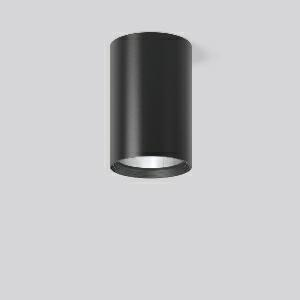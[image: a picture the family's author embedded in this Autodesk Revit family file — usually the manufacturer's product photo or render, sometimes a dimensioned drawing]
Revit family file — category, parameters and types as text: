
# Revit family: heledon_maxi_a_931230_003_4984
name_source: partatom
category: Lighting Fixtures
units: mm (PartAtom-declared; Revit-internal decimal feet)

## family parameters
Cut with Voids When Loaded = No
Host = Face
Light Source = No
Part Type = Normal
Room Calculation Point = No
Round Connector Dimension = Use Diameter
Shared = No

## types (1)
- HELEDON maxi A (1 x LED Modul 932 fresh meat, 2100 lm, 3200)
    Apparent Load = 33 VA
    Approval mark = CE
    CIE Flux Codes = 100 100 100 100 100
    Color Rendering = 90
    Color Temperature = 3200
    Default Elevation = 1800 mm
    Description = Series: HELEDON maxi
Cylindrical surface-mounted downlight. Housing: die-cast aluminium, powder-coated. Internal ceiling frame polycarbonate with bayonet mounting. Black plastic ring and recessed LED to prevent glare from the side. Optical assembly with reflector made of MIRO-Silver with 98% total light reflection for outstanding efficiency - can be changed without tools. Special LED for illumination of meat included. Suitable for Ceiling mounting. Easy installation with a separate ceiling frame with bayonet mounting and plug connection. Driver integrated. Connected via plug-in connector. High quality converter without flickering and stroboscopic effect. The following accessories can be mounted without use of tools: interchangeable lenses, decorative glasses, honeycomb louvre, clear and frosted diffusers, white interchangeable plastic ring. 
Colour: deep black, matt (RAL 9005)
Diameter: 123 mm
Height: 183 mm
Lamp: LED
Socket: without socket
Colour temperature: fresh meat
System power: 33 W
Rated luminous flux: 2100 lm
Luminous efficiency: 64 lm/W
Control gear: Regulated power supply
Protection class: I
Type of protection: IP 20
    Height = 183 mm
    Lamp = 1 x LED Modul 932 fresh meat
    Lamp Light Flux = 2100 lm
    Lamp count = 1
    Length = 123 mm
    Lifetime = 50000 h
    Luminous efficacy = 64 lm/W
    Manufacturer = RZB
    ModVariant = No
    Model = 931230.003
    Mounting Place = Ceiling
    Mounting Type = Surface mounted
    Number of Poles = 1
    OnlyDefault = Yes
    Power Factor = 1
    Product Name = HELEDON maxi A
    Product group = Surface mounted downlights
    ProductGroupID = 302
    Protection Class = Protection class I
    Protection Degree = IP 20
    RLX_Detail_Level = 1
    RLX_Emergency_Light_Flux = 0 lm
    RLX_Emergency_Type = 0
    RLX_Emergency_Type_DB = No
    RlxData = <blob elided: 96753 chars, md5=6b479a37>
    Socket = socket
    Standby Power = 0 W
    System Light Flux = 2100 lm
    System Power = 33 W
    Type Comments = Product without accessories
    Type Image = 931192.003.jpg
    URL = http://relux.com
    VarID = ---
    Voltage = 230 V
    Voltage Range = 220-240 V
    Weight = 0.00 kg
    Width = 0 mm  [stored 0 ft]

note: [stored X ft] marks values corroborated as IEEE doubles in the binary element streams (Revit-internal decimal feet)

## geometry (parser evidence)
native form markers: Blend x4, Sweep x9
no freeform markers — native parametric forms only
